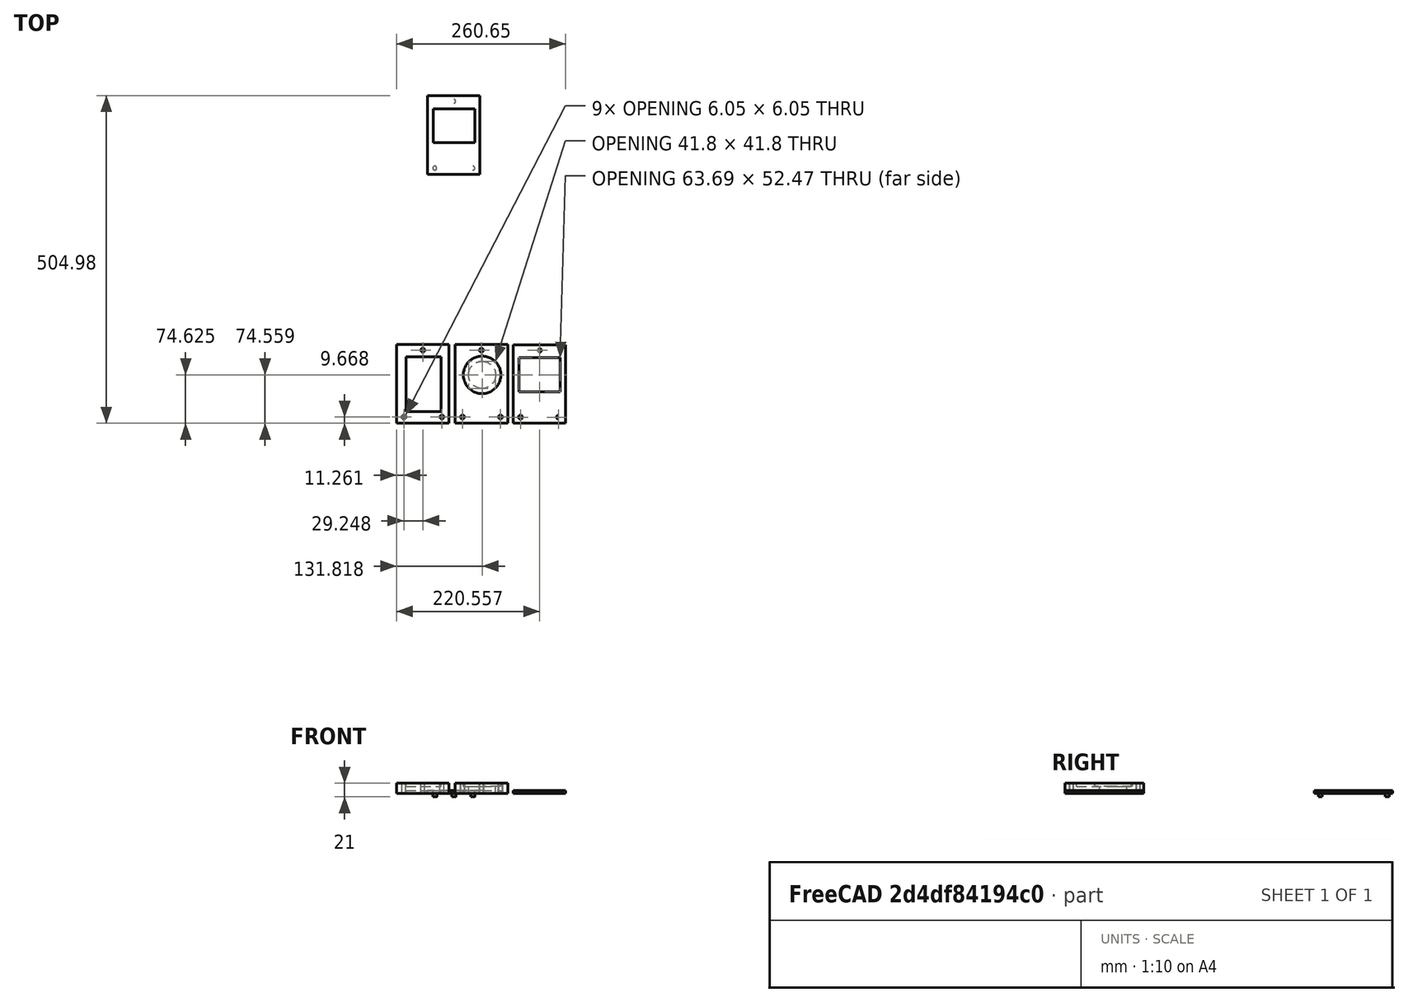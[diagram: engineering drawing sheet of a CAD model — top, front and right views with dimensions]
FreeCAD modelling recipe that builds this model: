
FCSTD DOCUMENT  (FreeCAD 0.17R10101 (Git))
Label: imaging_platfo
License: All rights reserved
LicenseURL: http://en.wikipedia.org/wiki/All_rights_reserved
objects: Part::Extrusion×27, Part::Feature×26, Part::Cut×7, Part::Fuse×6
note: 66 computed .brp shape members not serialized (recipe doc carries the construction recipe); baked Part::Feature solids carry a one-line shape summary decoded from their .brp

FEATURE [Part::Feature] rect3906
  shape: bbox 84.28 x 54.06 x 2e-07 mm, 0 faces, 0 solids (baked)
FEATURE [Part::Feature] path3910
  shape: bbox 16.19 x 16.19 x 2.17e-07 mm, 0 faces, 0 solids (baked)
FEATURE [Part::Feature] rect3912
  shape: bbox 17.93 x 4.914 x 2e-07 mm, 0 faces, 0 solids (baked)
FEATURE [Part::Feature] path3914
  shape: bbox 8.007 x 8.007 x 2e-07 mm, 0 faces, 0 solids (baked)
FEATURE [Part::Feature] path3916
  shape: bbox 4.004 x 4.004 x 2e-07 mm, 0 faces, 0 solids (baked)
FEATURE [Part::Feature] path3918
  shape: bbox 29.21 x 29.21 x 2e-07 mm, 0 faces, 0 solids (baked)
FEATURE [Part::Feature] path3023_81
  shape: bbox 6.047 x 6.047 x 2e-07 mm, 0 faces, 0 solids (baked)
FEATURE [Part::Feature] rect3906_7
  shape: bbox 54.06 x 84.28 x 2e-07 mm, 0 faces, 0 solids (baked)
FEATURE [Part::Feature] path3023_81_4
  shape: bbox 6.047 x 6.047 x 2e-07 mm, 0 faces, 0 solids (baked)
FEATURE [Part::Feature] path3023_81_8
  shape: bbox 6.047 x 6.047 x 2e-07 mm, 0 faces, 0 solids (baked)
FEATURE [Part::Feature] rect3014
  shape: bbox 80.98 x 121 x 2e-07 mm, 0 faces, 0 solids (baked)
FEATURE [Part::Feature] path2987_5_4_1_3
  shape: bbox 57.74 x 57.74 x 2.601e-07 mm, 0 faces, 0 solids (baked)
FEATURE [Part::Feature] path3023_81_2
  shape: bbox 6.047 x 6.047 x 2e-07 mm, 0 faces, 0 solids (baked)
FEATURE [Part::Feature] path3023_81_4_9
  shape: bbox 6.047 x 6.047 x 2e-07 mm, 0 faces, 0 solids (baked)
FEATURE [Part::Feature] path3023_81_8_6
  shape: bbox 6.047 x 6.047 x 2e-07 mm, 0 faces, 0 solids (baked)
FEATURE [Part::Feature] rect3014_38
  shape: bbox 80.98 x 121 x 2e-07 mm, 0 faces, 0 solids (baked)
FEATURE [Part::Feature] path2987_5_4_1_3_5
  shape: bbox 41.8 x 41.8 x 2e-07 mm, 0 faces, 0 solids (baked)
FEATURE [Part::Feature] path3023_81_2_0
  shape: bbox 6.047 x 6.047 x 2e-07 mm, 0 faces, 0 solids (baked)
FEATURE [Part::Feature] path3023_81_4_9_6
  shape: bbox 6.047 x 6.047 x 2e-07 mm, 0 faces, 0 solids (baked)
FEATURE [Part::Feature] path3023_81_8_6_8
  shape: bbox 6.047 x 6.047 x 2e-07 mm, 0 faces, 0 solids (baked)
FEATURE [Part::Feature] rect3014_38_0
  shape: bbox 121 x 80.98 x 2e-07 mm, 0 faces, 0 solids (baked)
FEATURE [Part::Extrusion] Extrude
  Base = -> rect3014
  Dir = (0,0,1)
  DirMode = 2
  FaceMakerClass = Part::FaceMakerBullseye
  LengthFwd = 16
  LengthRev = 0
  Solid = true
  Symmetric = false
FEATURE [Part::Extrusion] Extrude001
  Base = -> path3023_81
  Dir = (0,0,1)
  DirMode = 2
  FaceMakerClass = Part::FaceMakerBullseye
  LengthFwd = 16
  LengthRev = 0
  Solid = true
  Symmetric = false
FEATURE [Part::Extrusion] Extrude002
  Base = -> path3023_81_4
  Dir = (0,0,1)
  DirMode = 2
  FaceMakerClass = Part::FaceMakerBullseye
  LengthFwd = 16
  LengthRev = 0
  Solid = true
  Symmetric = false
FEATURE [Part::Extrusion] Extrude003
  Base = -> path3023_81_8
  Dir = (0,0,1)
  DirMode = 2
  FaceMakerClass = Part::FaceMakerBullseye
  LengthFwd = 16
  LengthRev = 0
  Solid = true
  Symmetric = false
FEATURE [Part::Fuse] Fusion
  Base = -> Extrude001
  Tool = -> Extrude002
FEATURE [Part::Fuse] Fusion001
  Base = -> Extrude003
  Tool = -> Fusion
FEATURE [Part::Cut] Cut
  Base = -> Extrude
  Tool = -> Fusion001
FEATURE [Part::Extrusion] Extrude004
  Base = -> rect3906_7
  Dir = (0,0,1)
  DirMode = 2
  FaceMakerClass = Part::FaceMakerBullseye
  LengthFwd = 5
  LengthRev = 0
  Placement = pos=(0,0,11) rot=(0,0,1;0rad)
  Solid = true
  Symmetric = false
FEATURE [Part::Extrusion] Extrude005
  Base = -> rect3906_7
  Dir = (0,0,1)
  DirMode = 2
  FaceMakerClass = Part::FaceMakerBullseye
  LengthFwd = 5
  LengthRev = 0
  Solid = true
  Symmetric = false
FEATURE [Part::Cut] Cut001  label="base"
  Base = -> Cut
  Tool = -> Extrude004
FEATURE [Part::Extrusion] Extrude006
  Base = -> path3023_81_2
  Dir = (0,0,1)
  DirMode = 2
  FaceMakerClass = Part::FaceMakerBullseye
  LengthFwd = 16
  LengthRev = 0
  Solid = true
  Symmetric = false
FEATURE [Part::Extrusion] Extrude007
  Base = -> path3023_81_4_9
  Dir = (0,0,1)
  DirMode = 2
  FaceMakerClass = Part::FaceMakerBullseye
  LengthFwd = 16
  LengthRev = 0
  Solid = true
  Symmetric = false
FEATURE [Part::Extrusion] Extrude008
  Base = -> path3023_81_8_6
  Dir = (0,0,1)
  DirMode = 2
  FaceMakerClass = Part::FaceMakerBullseye
  LengthFwd = 16
  LengthRev = 0
  Solid = true
  Symmetric = false
FEATURE [Part::Extrusion] Extrude009
  Base = -> rect3014_38
  Dir = (0,0,1)
  DirMode = 2
  FaceMakerClass = Part::FaceMakerBullseye
  LengthFwd = 16
  LengthRev = 0
  Solid = true
  Symmetric = false
FEATURE [Part::Extrusion] Extrude010
  Base = -> path3023_81_2
  Dir = (0,0,1)
  DirMode = 2
  FaceMakerClass = Part::FaceMakerBullseye
  LengthFwd = 16
  LengthRev = 0
  Solid = true
  Symmetric = false
FEATURE [Part::Extrusion] Extrude011
  Base = -> path3023_81_4_9
  Dir = (0,0,1)
  DirMode = 2
  FaceMakerClass = Part::FaceMakerBullseye
  LengthFwd = 16
  LengthRev = 0
  Solid = true
  Symmetric = false
FEATURE [Part::Extrusion] Extrude012
  Base = -> path3023_81_8_6
  Dir = (0,0,1)
  DirMode = 2
  FaceMakerClass = Part::FaceMakerBullseye
  LengthFwd = 16
  LengthRev = 0
  Solid = true
  Symmetric = false
FEATURE [Part::Extrusion] Extrude013
  Base = -> rect3014_38
  Dir = (0,0,1)
  DirMode = 2
  FaceMakerClass = Part::FaceMakerBullseye
  LengthFwd = 16
  LengthRev = 0
  Solid = true
  Symmetric = false
FEATURE [Part::Extrusion] Extrude014
  Base = -> path2987_5_4_1_3_5
  Dir = (0,0,1)
  DirMode = 2
  FaceMakerClass = Part::FaceMakerBullseye
  LengthFwd = 16
  LengthRev = 0
  Solid = true
  Symmetric = false
FEATURE [Part::Fuse] Fusion002
  Base = -> Extrude006
  Tool = -> Extrude007
FEATURE [Part::Fuse] Fusion003
  Base = -> Extrude008
  Tool = -> Fusion002
FEATURE [Part::Cut] Cut002
  Base = -> Extrude009
  Tool = -> Fusion003
FEATURE [Part::Cut] Cut003
  Base = -> Cut002
  Tool = -> Extrude014
FEATURE [Part::Extrusion] Extrude015
  Base = -> path2987_5_4_1_3
  Dir = (0,0,1)
  DirMode = 2
  FaceMakerClass = Part::FaceMakerBullseye
  LengthFwd = 5
  LengthRev = 0
  Placement = pos=(0,0,11) rot=(0,0,1;0rad)
  Solid = true
  Symmetric = false
FEATURE [Part::Extrusion] Extrude016
  Base = -> path2987_5_4_1_3
  Dir = (0,0,1)
  DirMode = 2
  FaceMakerClass = Part::FaceMakerBullseye
  LengthFwd = 5
  LengthRev = 0
  Solid = true
  Symmetric = false
FEATURE [Part::Cut] Cut004  label="middle"
  Base = -> Cut003
  Tool = -> Extrude015
FEATURE [Part::Feature] path3023_81_2001
  shape: bbox 6.047 x 6.047 x 2e-07 mm, 0 faces, 0 solids (baked)
FEATURE [Part::Feature] path3023_81_4_9001
  shape: bbox 6.047 x 6.047 x 2e-07 mm, 0 faces, 0 solids (baked)
FEATURE [Part::Feature] path3023_81_8_6001
  shape: bbox 6.047 x 6.047 x 2e-07 mm, 0 faces, 0 solids (baked)
FEATURE [Part::Feature] rect3014_38001
  shape: bbox 80.98 x 121 x 2e-07 mm, 0 faces, 0 solids (baked)
FEATURE [Part::Feature] rect3008_1
  shape: bbox 63.69 x 52.47 x 2e-07 mm, 0 faces, 0 solids (baked)
FEATURE [Part::Extrusion] Extrude017
  Base = -> path3023_81_2001
  Dir = (0,0,-1)
  DirMode = 2
  FaceMakerClass = Part::FaceMakerBullseye
  LengthFwd = 5
  LengthRev = 0
  Solid = true
  Symmetric = false
FEATURE [Part::Extrusion] Extrude018
  Base = -> path3023_81_4_9001
  Dir = (0,0,-1)
  DirMode = 2
  FaceMakerClass = Part::FaceMakerBullseye
  LengthFwd = 5
  LengthRev = 0
  Solid = true
  Symmetric = false
FEATURE [Part::Extrusion] Extrude019
  Base = -> path3023_81_8_6001
  Dir = (0,0,-1)
  DirMode = 2
  FaceMakerClass = Part::FaceMakerBullseye
  LengthFwd = 5
  LengthRev = 0
  Solid = true
  Symmetric = false
FEATURE [Part::Extrusion] Extrude020
  Base = -> rect3014_38001
  Dir = (0,0,1)
  DirMode = 2
  FaceMakerClass = Part::FaceMakerBullseye
  LengthFwd = 5
  LengthRev = 0
  Solid = true
  Symmetric = false
FEATURE [Part::Extrusion] Extrude021
  Base = -> rect3008_1
  Dir = (0,0,1)
  DirMode = 2
  FaceMakerClass = Part::FaceMakerBullseye
  LengthFwd = 5
  LengthRev = 0
  Solid = true
  Symmetric = false
FEATURE [Part::Extrusion] Extrude022
  Base = -> path3023_81_2001
  Dir = (0,0,-1)
  DirMode = 2
  FaceMakerClass = Part::FaceMakerBullseye
  LengthFwd = 5
  LengthRev = 0
  Solid = true
  Symmetric = false
FEATURE [Part::Extrusion] Extrude023
  Base = -> path3023_81_4_9001
  Dir = (0,0,-1)
  DirMode = 2
  FaceMakerClass = Part::FaceMakerBullseye
  LengthFwd = 5
  LengthRev = 0
  Solid = true
  Symmetric = false
FEATURE [Part::Extrusion] Extrude024
  Base = -> path3023_81_8_6001
  Dir = (0,0,-1)
  DirMode = 2
  FaceMakerClass = Part::FaceMakerBullseye
  LengthFwd = 5
  LengthRev = 0
  Solid = true
  Symmetric = false
FEATURE [Part::Extrusion] Extrude025
  Base = -> rect3014_38001
  Dir = (0,0,1)
  DirMode = 2
  FaceMakerClass = Part::FaceMakerBullseye
  LengthFwd = 5
  LengthRev = 0
  Solid = true
  Symmetric = false
FEATURE [Part::Extrusion] Extrude026
  Base = -> rect3008_1
  Dir = (0,0,1)
  DirMode = 2
  FaceMakerClass = Part::FaceMakerBullseye
  LengthFwd = 5
  LengthRev = 0
  Solid = true
  Symmetric = false
FEATURE [Part::Fuse] Fusion004
  Base = -> Extrude022
  Tool = -> Extrude023
FEATURE [Part::Fuse] Fusion005
  Base = -> Extrude024
  Placement = pos=(0,0,5) rot=(0,0,1;0rad)
  Tool = -> Fusion004
FEATURE [Part::Cut] Cut005
  Base = -> Extrude025
  Tool = -> Fusion005
FEATURE [Part::Cut] Cut006  label="top"
  Base = -> Cut005
  Placement = pos=(132,-384,0) rot=(0,0,1;0rad)
  Tool = -> Extrude026
